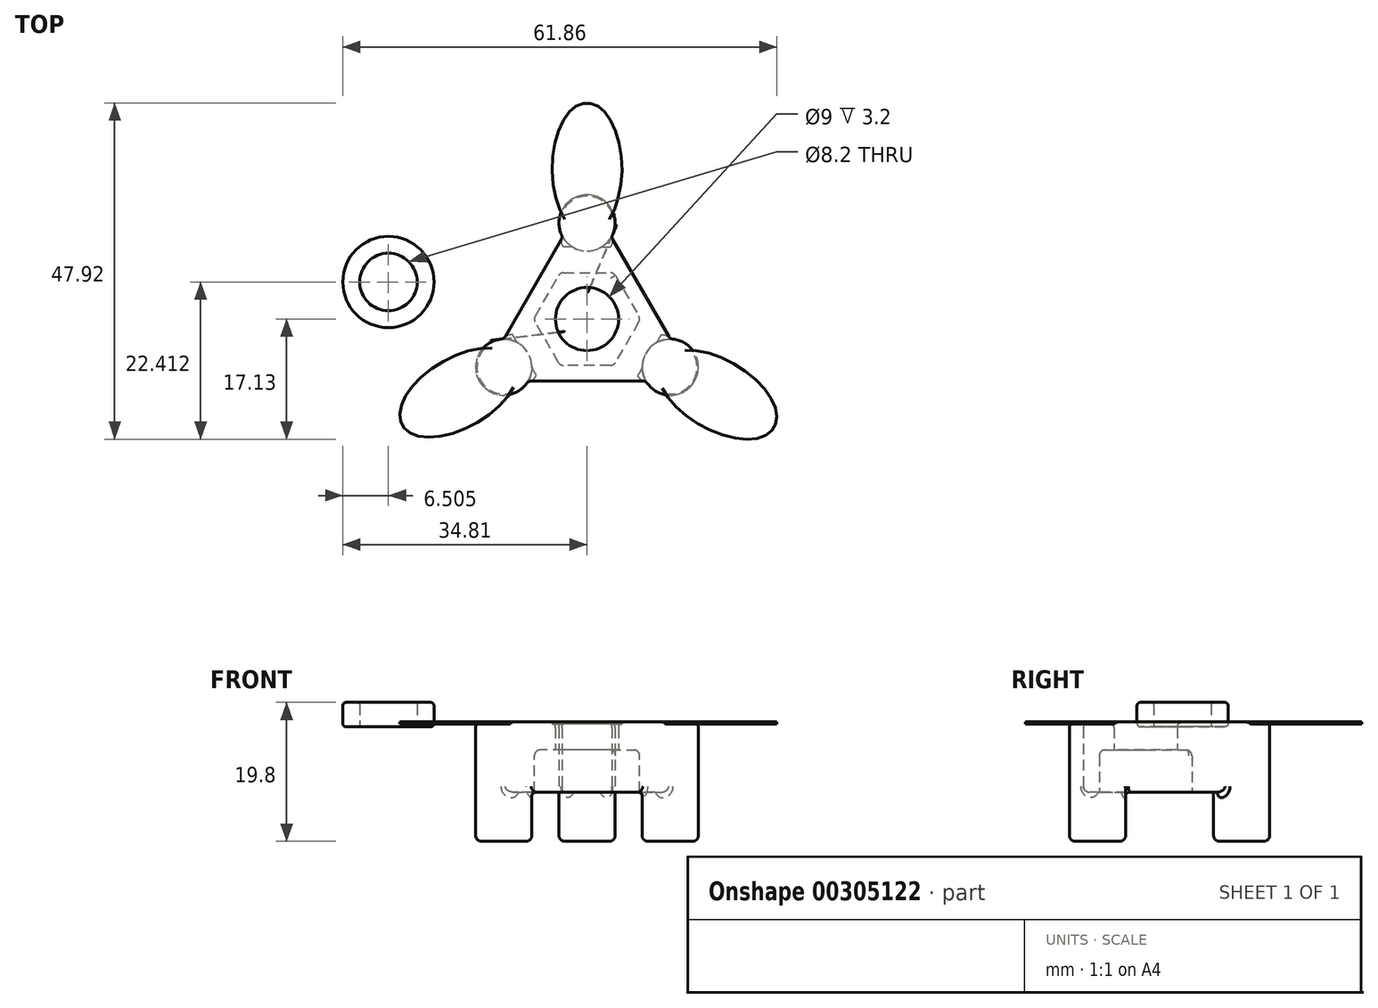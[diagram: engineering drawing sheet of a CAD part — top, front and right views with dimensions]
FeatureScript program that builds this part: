
annotation { "Feature Type Name" : "Feature", "Feature Type Description" : "" }
export const myFeature = defineFeature(function(context is Context, id is Id, definition is map)
    precondition{}
    {
        {
            var Q0;
            Q0=qCreatedBy(makeId("Top.planeOp"),FACE);
            var sketch = newSketch(context, id + "F0", { "sketchPlane" : qUnion([Q0])});
            skArc(sketch, "E0.cCircle", {"start": v(-20, -6.3) * mm, "mid": v(-22, -6.45) * mm, "end": v(-23.96, -6.88) * mm, "construction": true});
            skLineSegment(sketch, "E0.0", {"start": v(-28.4, -28.85) * mm, "end": v(-31.86, -26.85) * mm});
            skLineSegment(sketch, "E0.1", {"start": v(-31.86, -26.85) * mm, "end": v(-31.86, -22.85) * mm});
            skLineSegment(sketch, "E0.2", {"start": v(-23.46, -8.3) * mm, "end": v(-20, -6.3) * mm});
            skLineSegment(sketch, "E0.3", {"start": v(-20, -6.3) * mm, "end": v(-16.54, -8.3) * mm});
            skLineSegment(sketch, "E0.4", {"start": v(-8.14, -22.85) * mm, "end": v(-8.14, -26.85) * mm});
            skLineSegment(sketch, "E0.5", {"start": v(-8.14, -26.85) * mm, "end": v(-11.6, -28.85) * mm});
            skCircle(sketch, "E1", {"center": v(-20, -6.3) * mm, "radius": 4 * mm});
            skCircle(sketch, "E2", {"center": v(-8.14, -26.85) * mm, "radius": 4 * mm});
            skCircle(sketch, "E3", {"center": v(-31.86, -26.85) * mm, "radius": 4 * mm});
            skCircle(sketch, "E4", {"center": v(-20, -20) * mm, "radius": 4.5 * mm});
            skCircle(sketch, "E5", {"center": v(-20, -20) * mm, "radius": 6 * mm});
            skPoint(sketch, "E6.orphan", {"position": v(-8.14, -13.15) * mm});
            skCircle(sketch, "E7.cCircle", {"center": v(-20, -20) * mm, "radius": 6.6 * mm, "construction": true});
            skLineSegment(sketch, "E7.0", {"start": v(-23.81, -13.4) * mm, "end": v(-16.19, -13.4) * mm});
            skLineSegment(sketch, "E7.1", {"start": v(-16.19, -13.4) * mm, "end": v(-12.38, -20) * mm});
            skLineSegment(sketch, "E7.2", {"start": v(-12.38, -20) * mm, "end": v(-16.19, -26.6) * mm});
            skLineSegment(sketch, "E7.3", {"start": v(-16.19, -26.6) * mm, "end": v(-23.81, -26.6) * mm});
            skLineSegment(sketch, "E7.4", {"start": v(-23.81, -26.6) * mm, "end": v(-27.62, -20) * mm});
            skLineSegment(sketch, "E7.5", {"start": v(-27.62, -20) * mm, "end": v(-23.81, -13.4) * mm});
            skPoint(sketch, "E7.0.midPoint", {"position": v(-20, -13.4) * mm});
            skCircle(sketch, "E8.cCircle", {"center": v(-20, -20) * mm, "radius": 8.5 * mm, "construction": true});
            skLineSegment(sketch, "E8.0", {"start": v(-24.9, -11.5) * mm, "end": v(-15.1, -11.5) * mm});
            skLineSegment(sketch, "E8.1", {"start": v(-15.1, -11.5) * mm, "end": v(-10.19, -20) * mm});
            skLineSegment(sketch, "E8.2", {"start": v(-10.19, -20) * mm, "end": v(-15.1, -28.5) * mm});
            skLineSegment(sketch, "E8.3", {"start": v(-15.1, -28.5) * mm, "end": v(-24.9, -28.5) * mm});
            skLineSegment(sketch, "E8.4", {"start": v(-24.9, -28.5) * mm, "end": v(-29.81, -20) * mm});
            skLineSegment(sketch, "E8.5", {"start": v(-29.81, -20) * mm, "end": v(-24.9, -11.5) * mm});
            skPoint(sketch, "E8.0.midPoint", {"position": v(-20, -11.5) * mm});
            skLineSegment(sketch, "E9", {"start": v(-16.54, -8.3) * mm, "end": v(-8.14, -22.85) * mm});
            skLineSegment(sketch, "E10", {"start": v(-11.6, -28.85) * mm, "end": v(-28.4, -28.85) * mm});
            skLineSegment(sketch, "E11", {"start": v(-31.86, -22.85) * mm, "end": v(-23.46, -8.3) * mm});
            skCircle(sketch, "E12", {"center": v(-48.3, -14.72) * mm, "radius": 4.1 * mm});
            skCircle(sketch, "E13", {"center": v(-48.3, -14.72) * mm, "radius": 6.5 * mm});
            skSolve(sketch);
        }
        {
            var Q0;
            Q0=makeQuery(id+"F0.imprint","IMPRINT",FACE,{"disambiguationData":[TD([[makeQuery(id+"F0.imprint","IMPRINT",EDGE,{"derivedFrom":sQuery(id+"F0.wireOp",EDGE,"E12")}),-1.0]])]});
            extrude(context, id + "F1", {"entities" : qUnion([Q0]), "depth" : 3.5 * mm});
        }
        {
            var Q0;
            Q0=makeQuery(id+"F0.imprint","IMPRINT",FACE,{"disambiguationData":[TD([[makeQuery(id+"F0.imprint","IMPRINT",EDGE,{"derivedFrom":sQuery(id+"F0.wireOp",EDGE,"E7.0")}),1.0]])]});
            var Q1;
            Q1=makeQuery(id+"F0.imprint","IMPRINT",FACE,{"disambiguationData":[TD([[makeQuery(id+"F0.imprint","IMPRINT",EDGE,{"derivedFrom":sQuery(id+"F0.wireOp",EDGE,"E4")}),-1.0]])]});
            var Q2;
            Q2=makeQuery(id+"F0.imprint","IMPRINT",FACE,{"disambiguationData":[TD([[makeQuery(id+"F0.imprint","IMPRINT",EDGE,{"derivedFrom":sQuery(id+"F0.wireOp",EDGE,"E5")}),-1.0]])]});
            var Q3;
            {var subQ0=sQuery(id+"F0.wireOp",EDGE,"E0.2");Q3=makeQuery(id+"F0.imprint","IMPRINT",FACE,{"disambiguationData":[TD([[makeQuery(id+"F0.imprint","IMPRINT",EDGE,{"derivedFrom":subQ0}),-1.0]])]});}
            var Q4;
            {var subQ0=sQuery(id+"F0.wireOp",EDGE,"E0.2");Q4=makeQuery(id+"F0.imprint","IMPRINT",FACE,{"disambiguationData":[TD([[makeQuery(id+"F0.imprint","IMPRINT",EDGE,{"derivedFrom":subQ0}),1.0]])]});}
            var Q5;
            Q5=makeQuery(id+"F0.imprint","IMPRINT",FACE,{"disambiguationData":[TD([[makeQuery(id+"F0.imprint","IMPRINT",EDGE,{"derivedFrom":sQuery(id+"F0.wireOp",EDGE,"E8.0")}),1.0]])]});
            var Q6;
            {var subQ0=sQuery(id+"F0.wireOp",EDGE,"E0.0");Q6=makeQuery(id+"F0.imprint","IMPRINT",FACE,{"disambiguationData":[TD([[makeQuery(id+"F0.imprint","IMPRINT",EDGE,{"derivedFrom":subQ0}),1.0]])]});}
            var Q7;
            {var subQ0=sQuery(id+"F0.wireOp",EDGE,"E0.4");Q7=makeQuery(id+"F0.imprint","IMPRINT",FACE,{"disambiguationData":[TD([[makeQuery(id+"F0.imprint","IMPRINT",EDGE,{"derivedFrom":subQ0}),1.0]])]});}
            var Q8;
            {var subQ0=sQuery(id+"F0.wireOp",EDGE,"E0.4");Q8=makeQuery(id+"F0.imprint","IMPRINT",FACE,{"disambiguationData":[TD([[makeQuery(id+"F0.imprint","IMPRINT",EDGE,{"derivedFrom":subQ0}),-1.0]])]});}
            var Q9;
            {var subQ0=sQuery(id+"F0.wireOp",EDGE,"E0.0");Q9=makeQuery(id+"F0.imprint","IMPRINT",FACE,{"disambiguationData":[TD([[makeQuery(id+"F0.imprint","IMPRINT",EDGE,{"derivedFrom":subQ0}),-1.0]])]});}
            extrude(context, id + "F2", {"entities" : qUnion([Q0, Q1, Q2, Q3, Q4, Q5, Q6, Q7, Q8, Q9]), "depth" : 10 * mm});
        }
        {
            var Q0;
            Q0=makeQuery(id+"F0.imprint","IMPRINT",FACE,{"disambiguationData":[TD([[makeQuery(id+"F0.imprint","IMPRINT",EDGE,{"derivedFrom":sQuery(id+"F0.wireOp",EDGE,"E8.0")}),1.0]])]});
            var Q1;
            {var subQ0=sQuery(id+"F0.wireOp",EDGE,"E0.2");Q1=makeQuery(id+"F0.imprint","IMPRINT",FACE,{"disambiguationData":[TD([[makeQuery(id+"F0.imprint","IMPRINT",EDGE,{"derivedFrom":subQ0}),-1.0]])]});}
            var Q2;
            {var subQ0=sQuery(id+"F0.wireOp",EDGE,"E0.2");Q2=makeQuery(id+"F0.imprint","IMPRINT",FACE,{"disambiguationData":[TD([[makeQuery(id+"F0.imprint","IMPRINT",EDGE,{"derivedFrom":subQ0}),1.0]])]});}
            var Q3;
            {var subQ0=sQuery(id+"F0.wireOp",EDGE,"E0.0");Q3=makeQuery(id+"F0.imprint","IMPRINT",FACE,{"disambiguationData":[TD([[makeQuery(id+"F0.imprint","IMPRINT",EDGE,{"derivedFrom":subQ0}),-1.0]])]});}
            var Q4;
            {var subQ0=sQuery(id+"F0.wireOp",EDGE,"E0.0");Q4=makeQuery(id+"F0.imprint","IMPRINT",FACE,{"disambiguationData":[TD([[makeQuery(id+"F0.imprint","IMPRINT",EDGE,{"derivedFrom":subQ0}),1.0]])]});}
            var Q5;
            {var subQ0=sQuery(id+"F0.wireOp",EDGE,"E0.4");Q5=makeQuery(id+"F0.imprint","IMPRINT",FACE,{"disambiguationData":[TD([[makeQuery(id+"F0.imprint","IMPRINT",EDGE,{"derivedFrom":subQ0}),-1.0]])]});}
            var Q6;
            {var subQ0=sQuery(id+"F0.wireOp",EDGE,"E0.4");Q6=makeQuery(id+"F0.imprint","IMPRINT",FACE,{"disambiguationData":[TD([[makeQuery(id+"F0.imprint","IMPRINT",EDGE,{"derivedFrom":subQ0}),1.0]])]});}
            extrude(context, id + "F3", {"entities" : qUnion([Q0, Q1, Q2, Q3, Q4, Q5, Q6]), "operationType" : NewBodyOperationType.ADD, "depth" : 2.5 * mm});
        }
        {
            var Q0;
            Q0=makeQuery(id+"F0.imprint","IMPRINT",FACE,{"disambiguationData":[TD([[makeQuery(id+"F0.imprint","IMPRINT",EDGE,{"derivedFrom":sQuery(id+"F0.wireOp",EDGE,"E4")}),-1.0]])]});
            var Q1;
            Q1=makeQuery(id+"F0.imprint","IMPRINT",FACE,{"disambiguationData":[TD([[makeQuery(id+"F0.imprint","IMPRINT",EDGE,{"derivedFrom":sQuery(id+"F0.wireOp",EDGE,"E5")}),-1.0]])]});
            extrude(context, id + "F4", {"entities" : qUnion([Q0, Q1]), "operationType" : NewBodyOperationType.REMOVE, "depth" : 6 * mm});
        }
        {
            var Q0;
            {var subQ0=sQuery(id+"F0.wireOp",EDGE,"E0.4");Q0=makeQuery(id+"F0.imprint","IMPRINT",FACE,{"disambiguationData":[TD([[makeQuery(id+"F0.imprint","IMPRINT",EDGE,{"derivedFrom":subQ0}),-1.0]])]});}
            var Q1;
            {var subQ0=sQuery(id+"F0.wireOp",EDGE,"E0.2");Q1=makeQuery(id+"F0.imprint","IMPRINT",FACE,{"disambiguationData":[TD([[makeQuery(id+"F0.imprint","IMPRINT",EDGE,{"derivedFrom":subQ0}),-1.0]])]});}
            var Q2;
            {var subQ0=sQuery(id+"F0.wireOp",EDGE,"E0.2");Q2=makeQuery(id+"F0.imprint","IMPRINT",FACE,{"disambiguationData":[TD([[makeQuery(id+"F0.imprint","IMPRINT",EDGE,{"derivedFrom":subQ0}),1.0]])]});}
            var Q3;
            {var subQ0=sQuery(id+"F0.wireOp",EDGE,"E0.0");Q3=makeQuery(id+"F0.imprint","IMPRINT",FACE,{"disambiguationData":[TD([[makeQuery(id+"F0.imprint","IMPRINT",EDGE,{"derivedFrom":subQ0}),-1.0]])]});}
            var Q4;
            {var subQ0=sQuery(id+"F0.wireOp",EDGE,"E0.0");Q4=makeQuery(id+"F0.imprint","IMPRINT",FACE,{"disambiguationData":[TD([[makeQuery(id+"F0.imprint","IMPRINT",EDGE,{"derivedFrom":subQ0}),1.0]])]});}
            var Q5;
            {var subQ0=sQuery(id+"F0.wireOp",EDGE,"E0.4");Q5=makeQuery(id+"F0.imprint","IMPRINT",FACE,{"disambiguationData":[TD([[makeQuery(id+"F0.imprint","IMPRINT",EDGE,{"derivedFrom":subQ0}),1.0]])]});}
            extrude(context, id + "F5", {"entities" : qUnion([Q0, Q1, Q2, Q3, Q4, Q5]), "operationType" : NewBodyOperationType.ADD, "oppositeDirection" : true, "depth" : 7 * mm});
        }
        {
            var Q0;
            Q0=makeQuery(id+"F4.boolean.opBoolean","COPY",EDGE,{"derivedFrom":makeQuery(id+"F4.opExtrude","SWEPT_EDGE",EDGE,{"disambiguationData":[OSD([sQuery(id+"F0.wireOp",EDGE,"E7.1"),sQuery(id+"F0.wireOp",EDGE,"E7.2")])]})});
            var Q1;
            Q1=makeQuery(id+"F2.opExtrude","CAP_EDGE",EDGE,{"disambiguationData":[OSD([sQuery(id+"F0.wireOp",EDGE,"E10")])],"isStart":false});
            var Q2;
            Q2=makeQuery(id+"F2.opExtrude","CAP_EDGE",EDGE,{"disambiguationData":[OSD([sQuery(id+"F0.wireOp",EDGE,"E11")])],"isStart":true});
            var Q3;
            Q3=makeQuery(id+"F4.boolean.opBoolean","COPY",EDGE,{"derivedFrom":makeQuery(id+"F4.opExtrude","CAP_EDGE",EDGE,{"disambiguationData":[OSD([sQuery(id+"F0.wireOp",EDGE,"E7.2")])],"isStart":false})});
            var Q4;
            Q4=makeQuery(id+"F2.opExtrude","CAP_EDGE",EDGE,{"disambiguationData":[OSD([sQuery(id+"F0.wireOp",EDGE,"E9")])],"isStart":true});
            var Q5;
            Q5=makeQuery(id+"F4.boolean.opBoolean","COPY",EDGE,{"derivedFrom":makeQuery(id+"F4.opExtrude","CAP_EDGE",EDGE,{"disambiguationData":[OSD([sQuery(id+"F0.wireOp",EDGE,"E7.1")])],"isStart":false})});
            var Q6;
            Q6=makeQuery(id+"F4.boolean.opBoolean","COPY",EDGE,{"derivedFrom":makeQuery(id+"F4.opExtrude","SWEPT_EDGE",EDGE,{"disambiguationData":[OSD([sQuery(id+"F0.wireOp",EDGE,"E7.0"),sQuery(id+"F0.wireOp",EDGE,"E7.1")])]})});
            var Q7;
            Q7=makeQuery(id+"F4.boolean.opBoolean","COPY",EDGE,{"derivedFrom":makeQuery(id+"F4.opExtrude","CAP_EDGE",EDGE,{"disambiguationData":[OSD([sQuery(id+"F0.wireOp",EDGE,"E7.1")])],"isStart":true})});
            var Q8;
            Q8=makeQuery(id+"F2.opExtrude","CAP_EDGE",EDGE,{"disambiguationData":[OSD([sQuery(id+"F0.wireOp",EDGE,"E2")])],"isStart":false});
            var Q9;
            Q9=makeQuery(id+"F2.opExtrude","CAP_EDGE",EDGE,{"disambiguationData":[OSD([sQuery(id+"F0.wireOp",EDGE,"E11")])],"isStart":false});
            var Q10;
            Q10=makeQuery(id+"F5.opExtrude","CAP_EDGE",EDGE,{"disambiguationData":[OSD([sQuery(id+"F0.wireOp",EDGE,"E3")])],"isStart":false});
            var Q11;
            Q11=makeQuery(id+"F2.opExtrude","CAP_EDGE",EDGE,{"disambiguationData":[OSD([sQuery(id+"F0.wireOp",EDGE,"E4")])],"isStart":false});
            var Q12;
            Q12=makeQuery(id+"F5.opExtrude","CAP_EDGE",EDGE,{"disambiguationData":[OSD([sQuery(id+"F0.wireOp",EDGE,"E2")])],"isStart":false});
            var Q13;
            Q13=makeQuery(id+"F4.boolean.opBoolean","COPY",EDGE,{"derivedFrom":makeQuery(id+"F4.opExtrude","CAP_EDGE",EDGE,{"disambiguationData":[OSD([sQuery(id+"F0.wireOp",EDGE,"E7.5")])],"isStart":false})});
            var Q14;
            Q14=makeQuery(id+"F2.opExtrude","SWEPT_EDGE",EDGE,{"disambiguationData":[OSD([sQuery(id+"F0.wireOp",EDGE,"E0.1"),sQuery(id+"F0.wireOp",EDGE,"E3"),sQuery(id+"F0.wireOp",EDGE,"E11")])]});
            var Q15;
            Q15=makeQuery(id+"F5.opExtrude","CAP_EDGE",EDGE,{"disambiguationData":[OSD([sQuery(id+"F0.wireOp",EDGE,"E1")])],"isStart":true});
            var Q16;
            Q16=makeQuery(id+"F2.opExtrude","CAP_EDGE",EDGE,{"disambiguationData":[OSD([sQuery(id+"F0.wireOp",EDGE,"E10")])],"isStart":true});
            var Q17;
            Q17=makeQuery(id+"F4.boolean.opBoolean","COPY",EDGE,{"derivedFrom":makeQuery(id+"F4.opExtrude","CAP_EDGE",EDGE,{"disambiguationData":[OSD([sQuery(id+"F0.wireOp",EDGE,"E7.4")])],"isStart":true})});
            var Q18;
            Q18=makeQuery(id+"F4.boolean.opBoolean","COPY",EDGE,{"derivedFrom":makeQuery(id+"F4.opExtrude","CAP_EDGE",EDGE,{"disambiguationData":[OSD([sQuery(id+"F0.wireOp",EDGE,"E7.3")])],"isStart":true})});
            var Q19;
            Q19=makeQuery(id+"F2.opExtrude","SWEPT_EDGE",EDGE,{"disambiguationData":[OSD([sQuery(id+"F0.wireOp",EDGE,"E0.0"),sQuery(id+"F0.wireOp",EDGE,"E3"),sQuery(id+"F0.wireOp",EDGE,"E10")])]});
            var Q20;
            Q20=makeQuery(id+"F4.boolean.opBoolean","COPY",EDGE,{"derivedFrom":makeQuery(id+"F4.opExtrude","SWEPT_EDGE",EDGE,{"disambiguationData":[OSD([sQuery(id+"F0.wireOp",EDGE,"E7.0"),sQuery(id+"F0.wireOp",EDGE,"E7.5")])]})});
            var Q21;
            Q21=makeQuery(id+"F2.opExtrude","SWEPT_EDGE",EDGE,{"disambiguationData":[OSD([sQuery(id+"F0.wireOp",EDGE,"E0.2"),sQuery(id+"F0.wireOp",EDGE,"E1"),sQuery(id+"F0.wireOp",EDGE,"E11")])]});
            var Q22;
            Q22=makeQuery(id+"F5.opExtrude","CAP_EDGE",EDGE,{"disambiguationData":[OSD([sQuery(id+"F0.wireOp",EDGE,"E1")])],"isStart":false});
            var Q23;
            Q23=makeQuery(id+"F4.boolean.opBoolean","COPY",EDGE,{"derivedFrom":makeQuery(id+"F4.opExtrude","CAP_EDGE",EDGE,{"disambiguationData":[OSD([sQuery(id+"F0.wireOp",EDGE,"E7.0")])],"isStart":false})});
            var Q24;
            Q24=makeQuery(id+"F2.opExtrude","CAP_EDGE",EDGE,{"disambiguationData":[OSD([sQuery(id+"F0.wireOp",EDGE,"E9")])],"isStart":false});
            var Q25;
            Q25=makeQuery(id+"F4.boolean.opBoolean","COPY",EDGE,{"derivedFrom":makeQuery(id+"F4.opExtrude","CAP_EDGE",EDGE,{"disambiguationData":[OSD([sQuery(id+"F0.wireOp",EDGE,"E7.0")])],"isStart":true})});
            var Q26;
            Q26=makeQuery(id+"F4.boolean.opBoolean","COPY",EDGE,{"derivedFrom":makeQuery(id+"F4.opExtrude","CAP_EDGE",EDGE,{"disambiguationData":[OSD([sQuery(id+"F0.wireOp",EDGE,"E7.2")])],"isStart":true})});
            var Q27;
            Q27=makeQuery(id+"F4.boolean.opBoolean","COPY",EDGE,{"derivedFrom":makeQuery(id+"F4.opExtrude","CAP_EDGE",EDGE,{"disambiguationData":[OSD([sQuery(id+"F0.wireOp",EDGE,"E4")])],"isStart":false})});
            var Q28;
            Q28=makeQuery(id+"F2.opExtrude","SWEPT_EDGE",EDGE,{"disambiguationData":[OSD([sQuery(id+"F0.wireOp",EDGE,"E0.5"),sQuery(id+"F0.wireOp",EDGE,"E2"),sQuery(id+"F0.wireOp",EDGE,"E10")])]});
            var Q29;
            Q29=makeQuery(id+"F2.opExtrude","CAP_EDGE",EDGE,{"disambiguationData":[OSD([sQuery(id+"F0.wireOp",EDGE,"E3")])],"isStart":false});
            var Q30;
            Q30=makeQuery(id+"F4.boolean.opBoolean","COPY",EDGE,{"derivedFrom":makeQuery(id+"F4.opExtrude","CAP_EDGE",EDGE,{"disambiguationData":[OSD([sQuery(id+"F0.wireOp",EDGE,"E7.4")])],"isStart":false})});
            var Q31;
            Q31=makeQuery(id+"F4.boolean.opBoolean","COPY",EDGE,{"derivedFrom":makeQuery(id+"F4.opExtrude","SWEPT_EDGE",EDGE,{"disambiguationData":[OSD([sQuery(id+"F0.wireOp",EDGE,"E7.2"),sQuery(id+"F0.wireOp",EDGE,"E7.3")])]})});
            var Q32;
            Q32=makeQuery(id+"F2.opExtrude","CAP_EDGE",EDGE,{"disambiguationData":[OSD([sQuery(id+"F0.wireOp",EDGE,"E1")])],"isStart":false});
            var Q33;
            Q33=makeQuery(id+"F5.opExtrude","CAP_EDGE",EDGE,{"disambiguationData":[OSD([sQuery(id+"F0.wireOp",EDGE,"E3")])],"isStart":true});
            var Q34;
            Q34=makeQuery(id+"F4.boolean.opBoolean","COPY",EDGE,{"derivedFrom":makeQuery(id+"F4.opExtrude","CAP_EDGE",EDGE,{"disambiguationData":[OSD([sQuery(id+"F0.wireOp",EDGE,"E7.3")])],"isStart":false})});
            var Q35;
            Q35=makeQuery(id+"F4.boolean.opBoolean","COPY",EDGE,{"derivedFrom":makeQuery(id+"F4.opExtrude","SWEPT_EDGE",EDGE,{"disambiguationData":[OSD([sQuery(id+"F0.wireOp",EDGE,"E7.3"),sQuery(id+"F0.wireOp",EDGE,"E7.4")])]})});
            var Q36;
            Q36=makeQuery(id+"F4.boolean.opBoolean","COPY",EDGE,{"derivedFrom":makeQuery(id+"F4.opExtrude","CAP_EDGE",EDGE,{"disambiguationData":[OSD([sQuery(id+"F0.wireOp",EDGE,"E7.5")])],"isStart":true})});
            var Q37;
            Q37=makeQuery(id+"F5.opExtrude","CAP_EDGE",EDGE,{"disambiguationData":[OSD([sQuery(id+"F0.wireOp",EDGE,"E2")])],"isStart":true});
            var Q38;
            Q38=makeQuery(id+"F4.boolean.opBoolean","COPY",EDGE,{"derivedFrom":makeQuery(id+"F4.opExtrude","SWEPT_EDGE",EDGE,{"disambiguationData":[OSD([sQuery(id+"F0.wireOp",EDGE,"E7.4"),sQuery(id+"F0.wireOp",EDGE,"E7.5")])]})});
            var Q39;
            Q39=makeQuery(id+"F2.opExtrude","SWEPT_EDGE",EDGE,{"disambiguationData":[OSD([sQuery(id+"F0.wireOp",EDGE,"E0.3"),sQuery(id+"F0.wireOp",EDGE,"E1"),sQuery(id+"F0.wireOp",EDGE,"E9")])]});
            var Q40;
            Q40=makeQuery(id+"F2.opExtrude","SWEPT_EDGE",EDGE,{"disambiguationData":[OSD([sQuery(id+"F0.wireOp",EDGE,"E0.4"),sQuery(id+"F0.wireOp",EDGE,"E2"),sQuery(id+"F0.wireOp",EDGE,"E9")])]});
            fillet(context, id + "F6", {"entities" : qUnion([Q0, Q1, Q2, Q3, Q4, Q5, Q6, Q7, Q8, Q9, Q10, Q11, Q12, Q13, Q14, Q15, Q16, Q17, Q18, Q19, Q20, Q21, Q22, Q23, Q24, Q25, Q26, Q27, Q28, Q29, Q30, Q31, Q32, Q33, Q34, Q35, Q36, Q37, Q38, Q39, Q40]), "radius" : 0.8 * mm, "tangentPropagation" : true, "allowEdgeOverflow" : false});
        }
        {
            var Q0;
            Q0=makeQuery(id+"F1.opExtrude","SWEPT_FACE",FACE,{"disambiguationData":[OSD([sQuery(id+"F0.wireOp",EDGE,"E13")])]});
            fillet(context, id + "F7", {"entities" : qUnion([Q0]), "radius" : 0.5 * mm, "tangentPropagation" : true, "allowEdgeOverflow" : false});
        }
        {
            var Q0;
            Q0=makeQuery(id+"F2.opExtrude","CAP_FACE",FACE,{"disambiguationData":[OSD([sQuery(id+"F0.wireOp",EDGE,"E1"),sQuery(id+"F0.wireOp",EDGE,"E2"),sQuery(id+"F0.wireOp",EDGE,"E3"),sQuery(id+"F0.wireOp",EDGE,"E4"),sQuery(id+"F0.wireOp",EDGE,"E9"),sQuery(id+"F0.wireOp",EDGE,"E10"),sQuery(id+"F0.wireOp",EDGE,"E11")])],"isStart":false});
            var sketch = newSketch(context, id + "F8", { "sketchPlane" : qUnion([Q0])});
            skEllipse(sketch, "E14", {"center": v(-20, 1.45) * mm, "majorRadius": 9.34 * mm, "minorRadius": 4.98 * mm, "majorAxis": v(0, -1)});
            skPoint(sketch, "E14.centerSnap0", {"position": v(-20, -3.1) * mm});
            skEllipse(sketch, "E15", {"center": v(-1.41, -30.78) * mm, "majorRadius": 9.34 * mm, "minorRadius": 4.98 * mm, "majorAxis": v(-0.87, 0.5)});
            skEllipse(sketch, "E16", {"center": v(-38.23, -30.48) * mm, "majorRadius": 9.34 * mm, "minorRadius": 4.98 * mm, "majorAxis": v(-0.87, -0.5)});
            skSolve(sketch);
        }
        {
            var Q0;
            {var subQ0=sQuery(id+"F8.wireOp",EDGE,"E14");var subQ1=sQuery(id+"F0.wireOp",EDGE,"E1");var subQ2=makeQuery(id+"F6.opFillet","BLEND_EDGE",EDGE,{"blendedFrom":[makeQuery(id+"F2.opExtrude","CAP_EDGE",EDGE,{"disambiguationData":[OSD([subQ1])],"isStart":false}),makeQuery(id+"F2.opExtrude","CAP_FACE",FACE,{"disambiguationData":[OSD([subQ1,sQuery(id+"F0.wireOp",EDGE,"E2"),sQuery(id+"F0.wireOp",EDGE,"E3"),sQuery(id+"F0.wireOp",EDGE,"E4"),sQuery(id+"F0.wireOp",EDGE,"E9"),sQuery(id+"F0.wireOp",EDGE,"E10"),sQuery(id+"F0.wireOp",EDGE,"E11")])],"isStart":false})],"blendedInto":[makeQuery(id+"F2.opExtrude","CAP_FACE",FACE,{"disambiguationData":[OSD([subQ1,sQuery(id+"F0.wireOp",EDGE,"E2"),sQuery(id+"F0.wireOp",EDGE,"E3"),sQuery(id+"F0.wireOp",EDGE,"E4"),sQuery(id+"F0.wireOp",EDGE,"E9"),sQuery(id+"F0.wireOp",EDGE,"E10"),sQuery(id+"F0.wireOp",EDGE,"E11")])],"isStart":false})]});var subQ3=makeQuery(id+"F8.imprint","INTERSECT",VERTEX,{"disambiguationData":[OD(0.0)],"derivedFrom":[subQ2,subQ0]});Q0=makeQuery(id+"F8.imprint","IMPRINT",FACE,{"disambiguationData":[TD([[makeQuery(id+"F8.imprint","IMPRINT",EDGE,{"disambiguationData":[TD([[subQ3,1.0]])],"derivedFrom":subQ0}),1.0]])]});}
            var Q1;
            {var subQ0=sQuery(id+"F8.wireOp",EDGE,"E16");var subQ1=sQuery(id+"F0.wireOp",EDGE,"E3");var subQ2=makeQuery(id+"F6.opFillet","BLEND_EDGE",EDGE,{"blendedFrom":[makeQuery(id+"F2.opExtrude","CAP_EDGE",EDGE,{"disambiguationData":[OSD([subQ1])],"isStart":false}),makeQuery(id+"F2.opExtrude","CAP_FACE",FACE,{"disambiguationData":[OSD([sQuery(id+"F0.wireOp",EDGE,"E1"),sQuery(id+"F0.wireOp",EDGE,"E2"),subQ1,sQuery(id+"F0.wireOp",EDGE,"E4"),sQuery(id+"F0.wireOp",EDGE,"E9"),sQuery(id+"F0.wireOp",EDGE,"E10"),sQuery(id+"F0.wireOp",EDGE,"E11")])],"isStart":false})],"blendedInto":[makeQuery(id+"F2.opExtrude","CAP_FACE",FACE,{"disambiguationData":[OSD([sQuery(id+"F0.wireOp",EDGE,"E1"),sQuery(id+"F0.wireOp",EDGE,"E2"),subQ1,sQuery(id+"F0.wireOp",EDGE,"E4"),sQuery(id+"F0.wireOp",EDGE,"E9"),sQuery(id+"F0.wireOp",EDGE,"E10"),sQuery(id+"F0.wireOp",EDGE,"E11")])],"isStart":false})]});var subQ3=makeQuery(id+"F8.imprint","INTERSECT",VERTEX,{"disambiguationData":[OD(0.0)],"derivedFrom":[subQ2,subQ0]});Q1=makeQuery(id+"F8.imprint","IMPRINT",FACE,{"disambiguationData":[TD([[makeQuery(id+"F8.imprint","IMPRINT",EDGE,{"disambiguationData":[TD([[subQ3,1.0]])],"derivedFrom":subQ0}),1.0]])]});}
            var Q2;
            {var subQ0=sQuery(id+"F8.wireOp",EDGE,"E15");var subQ1=sQuery(id+"F0.wireOp",EDGE,"E2");var subQ2=makeQuery(id+"F6.opFillet","BLEND_EDGE",EDGE,{"blendedFrom":[makeQuery(id+"F2.opExtrude","CAP_EDGE",EDGE,{"disambiguationData":[OSD([subQ1])],"isStart":false}),makeQuery(id+"F2.opExtrude","CAP_FACE",FACE,{"disambiguationData":[OSD([sQuery(id+"F0.wireOp",EDGE,"E1"),subQ1,sQuery(id+"F0.wireOp",EDGE,"E3"),sQuery(id+"F0.wireOp",EDGE,"E4"),sQuery(id+"F0.wireOp",EDGE,"E9"),sQuery(id+"F0.wireOp",EDGE,"E10"),sQuery(id+"F0.wireOp",EDGE,"E11")])],"isStart":false})],"blendedInto":[makeQuery(id+"F2.opExtrude","CAP_FACE",FACE,{"disambiguationData":[OSD([sQuery(id+"F0.wireOp",EDGE,"E1"),subQ1,sQuery(id+"F0.wireOp",EDGE,"E3"),sQuery(id+"F0.wireOp",EDGE,"E4"),sQuery(id+"F0.wireOp",EDGE,"E9"),sQuery(id+"F0.wireOp",EDGE,"E10"),sQuery(id+"F0.wireOp",EDGE,"E11")])],"isStart":false})]});var subQ3=makeQuery(id+"F8.imprint","INTERSECT",VERTEX,{"disambiguationData":[OD(0.0)],"derivedFrom":[subQ2,subQ0]});Q2=makeQuery(id+"F8.imprint","IMPRINT",FACE,{"disambiguationData":[TD([[makeQuery(id+"F8.imprint","IMPRINT",EDGE,{"disambiguationData":[TD([[subQ3,1.0]])],"derivedFrom":subQ0}),1.0]])]});}
            extrude(context, id + "F9", {"entities" : qUnion([Q0, Q1, Q2]), "operationType" : NewBodyOperationType.ADD, "oppositeDirection" : true, "depth" : 0.3 * mm});
        }
        {
            var Q0;
            Q0=makeQuery(id+"F1.opExtrude","SWEPT_BODY",BODY,{"disambiguationData":[OSD([sQuery(id+"F0.wireOp",EDGE,"E12"),sQuery(id+"F0.wireOp",EDGE,"E13")])]});
            transform(context, id + "F10", {"entities" : qUnion([Q0]), "transformType" : TransformType.TRANSLATION_3D, "dx" : 0 * mm, "dy" : 0 * mm, "dz" : 9.3 * mm, "makeCopy" : false});
        }
        {
            var Q0;
            Q0=makeQuery(id+"F1.opExtrude","SWEPT_FACE",FACE,{"disambiguationData":[OSD([sQuery(id+"F0.wireOp",EDGE,"E12")])]});
            fillet(context, id + "F11", {"entities" : qUnion([Q0]), "radius" : 0.3 * mm, "tangentPropagation" : true, "allowEdgeOverflow" : false});
        }
    });
